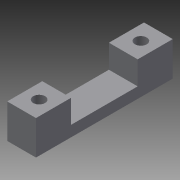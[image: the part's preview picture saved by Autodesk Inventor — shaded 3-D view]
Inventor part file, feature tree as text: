
AUTODESK INVENTOR PART (.ipt)
format: ipt  version: 2013 SP2 (Build 170200200, 200)  size: 96,256 bytes
history: native  units: mm
features: extrude x3, sketch x3, projected_geometry x1
ambient origin geometry x8: Origin, YZ Plane, XZ Plane, XY Plane, X Axis, Y Axis, Z Axis, Center Point
bodies: Solid1 (feature_tree)
feature tree (7):
  extrude  "Extrusion1"  Depth=8.0mm
  extrude  "Extrusion2"  Depth=9.75mm
  extrude  "Extrusion3"  Depth=6.5mm TaperAngle=0.0deg
  sketch  "Sketch1"  dims[d0=38.0mm d2=8.0mm]
  sketch  "Sketch2"  dims[d3=3.0mm d4=0.0mm d5=9.75mm]
  sketch  "Sketch3"  dims[d7=9.75mm d8=6.5mm d9=0.0mm d10=3.3mm d12=0.0mm d13=0.0mm]
  projected_geometry  "Projected Loop1"
